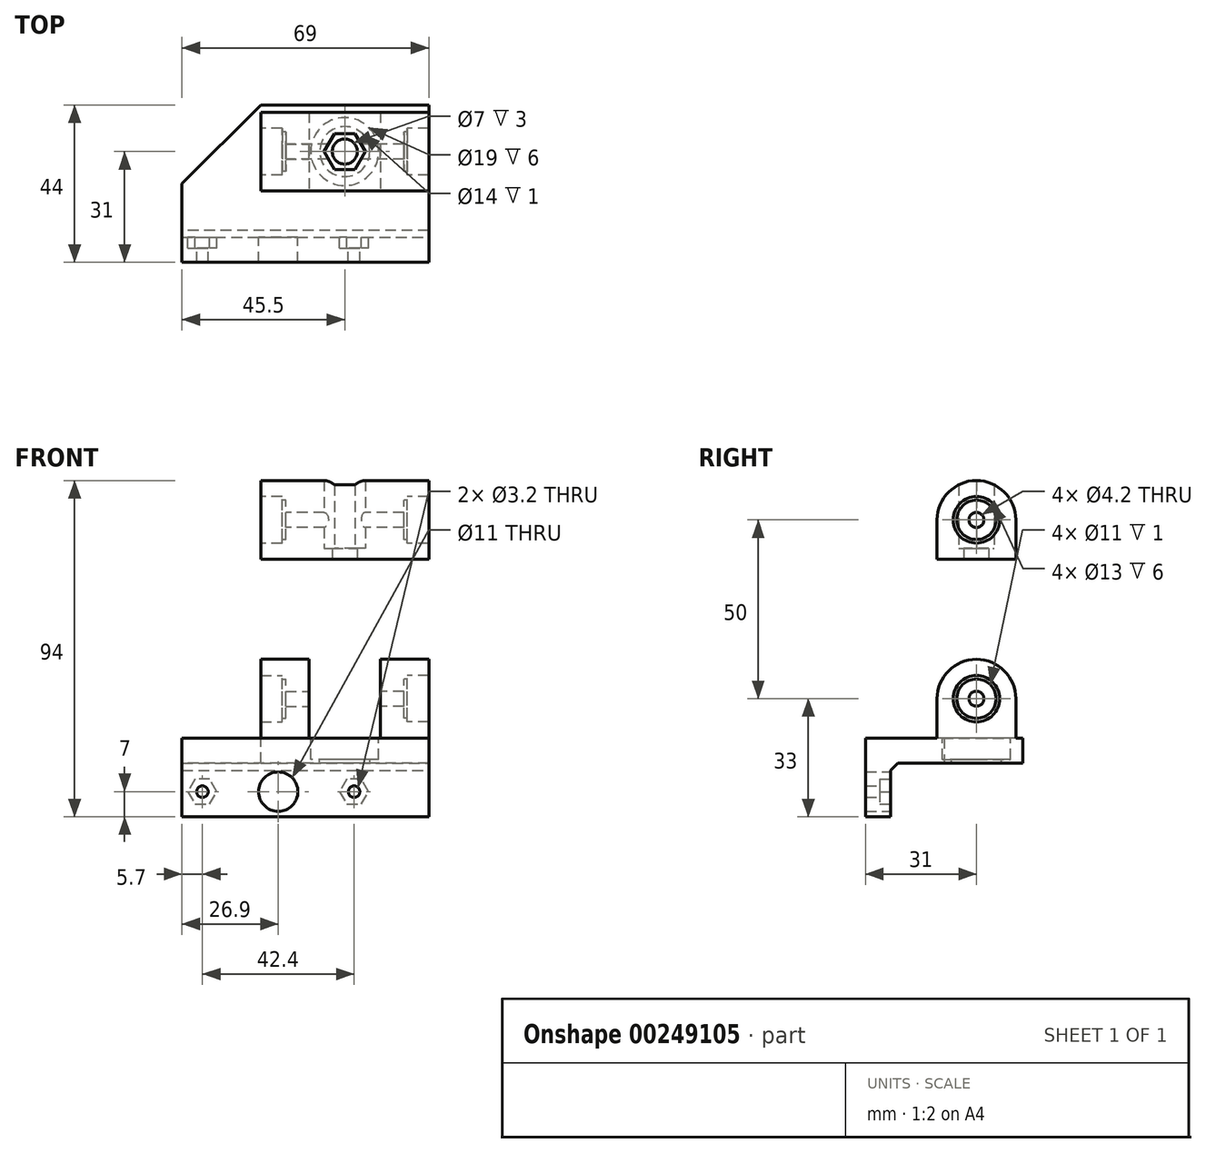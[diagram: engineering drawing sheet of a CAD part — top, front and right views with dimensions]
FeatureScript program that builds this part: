
annotation { "Feature Type Name" : "Feature", "Feature Type Description" : "" }
export const myFeature = defineFeature(function(context is Context, id is Id, definition is map)
    precondition{}
    {
        {
            var Q0;
            Q0=qCreatedBy(makeId("Top.planeOp"),FACE);
            var sketch = newSketch(context, id + "F0", { "sketchPlane" : qUnion([Q0])});
            skLineSegment(sketch, "E0", {"start": v(0, 0) * mm, "end": v(-23.5, 0) * mm, "construction": true});
            skLineSegment(sketch, "E1", {"start": v(0, 0) * mm, "end": v(23.5, 0) * mm, "construction": true});
            skLineSegment(sketch, "E2", {"start": v(-23.5, 0) * mm, "end": v(-23.5, -31) * mm});
            skLineSegment(sketch, "E3", {"start": v(-23.5, -31) * mm, "end": v(23.5, -31) * mm});
            skLineSegment(sketch, "E4", {"start": v(23.5, -31) * mm, "end": v(23.5, 0) * mm});
            skLineSegment(sketch, "E5", {"start": v(-23.5, 0) * mm, "end": v(-23.5, 13) * mm});
            skLineSegment(sketch, "E6", {"start": v(-23.5, 13) * mm, "end": v(23.5, 13) * mm});
            skLineSegment(sketch, "E7", {"start": v(23.5, 13) * mm, "end": v(23.5, 0) * mm});
            skCircle(sketch, "E8", {"center": v(0, 0) * mm, "radius": 9.5 * mm});
            skCircle(sketch, "E9", {"center": v(0, 0) * mm, "radius": 7 * mm});
            skLineSegment(sketch, "E10", {"start": v(0, 16.88) * mm, "end": v(-15, 16.88) * mm, "construction": true});
            skSolve(sketch);
        }
        {
            var Q0;
            Q0=makeQuery(id+"F0.imprint","IMPRINT",FACE,{"disambiguationData":[TD([[makeQuery(id+"F0.imprint","IMPRINT",EDGE,{"derivedFrom":sQuery(id+"F0.wireOp",EDGE,"E2")}),1.0]])]});
            extrude(context, id + "F1", {"entities" : qUnion([Q0]), "oppositeDirection" : true, "depth" : 7 * mm});
        }
        {
            var Q0;
            Q0=makeQuery(id+"F0.imprint","IMPRINT",FACE,{"disambiguationData":[TD([[makeQuery(id+"F0.imprint","IMPRINT",EDGE,{"derivedFrom":sQuery(id+"F0.wireOp",EDGE,"E8")}),1.0]])]});
            extrude(context, id + "F2", {"entities" : qUnion([Q0]), "operationType" : NewBodyOperationType.ADD, "oppositeDirection" : true, "depth" : 7 * mm, "hasSecondDirection" : true, "secondDirectionOppositeDirection" : true, "secondDirectionDepth" : 6 * mm});
        }
        {
            var Q0;
            {var subQ0=sQuery(id+"F0.wireOp",EDGE,"E8");Q0=makeQuery(id+"F2.boolean.opBoolean","MERGE",FACE,{"derivedFrom":[makeQuery(id+"F1.opExtrude","CAP_FACE",FACE,{"disambiguationData":[OSD([sQuery(id+"F0.wireOp",EDGE,"E2"),sQuery(id+"F0.wireOp",EDGE,"E3"),sQuery(id+"F0.wireOp",EDGE,"E4"),sQuery(id+"F0.wireOp",EDGE,"E5"),sQuery(id+"F0.wireOp",EDGE,"E6"),sQuery(id+"F0.wireOp",EDGE,"E7"),subQ0])],"isStart":false}),makeQuery(id+"F2.opExtrude","CAP_FACE",FACE,{"disambiguationData":[OSD([subQ0,sQuery(id+"F0.wireOp",EDGE,"E9")])],"isStart":false})]});}
            var sketch = newSketch(context, id + "F3", { "sketchPlane" : qUnion([Q0])});
            skLineSegment(sketch, "E11.bottom", {"start": v(-23.5, 31) * mm, "end": v(23.5, 31) * mm});
            skLineSegment(sketch, "E11.top", {"start": v(-23.5, 24) * mm, "end": v(23.5, 24) * mm});
            skLineSegment(sketch, "E11.left", {"start": v(-23.5, 31) * mm, "end": v(-23.5, 24) * mm});
            skLineSegment(sketch, "E11.right", {"start": v(23.5, 31) * mm, "end": v(23.5, 24) * mm});
            skSolve(sketch);
        }
        {
            var Q0;
            Q0 = qSketchRegion(id + "F3", true);
            extrude(context, id + "F4", {"entities" : qUnion([Q0]), "operationType" : NewBodyOperationType.ADD, "depth" : 14 * mm});
        }
        {
            var Q0;
            Q0=makeQuery(id+"F4.opExtrude","SWEPT_FACE",FACE,{"disambiguationData":[OSD([sQuery(id+"F3.wireOp",EDGE,"E11.top")])]});
            var sketch = newSketch(context, id + "F5", { "sketchPlane" : qUnion([Q0])});
            skCircle(sketch, "E12", {"center": v(18.6, -15) * mm, "radius": 4.85 * mm});
            skCircle(sketch, "E13", {"center": v(39.8, -15) * mm, "radius": 1.6 * mm});
            skCircle(sketch, "E14", {"center": v(-2.6, -15) * mm, "radius": 1.6 * mm});
            skCircle(sketch, "E15", {"center": v(18.6, -15) * mm, "radius": 5.5 * mm});
            skSolve(sketch);
        }
        {
            var Q0;
            Q0=makeQuery(id+"F4.boolean.opBoolean","MERGE",FACE,{"derivedFrom":[makeQuery(id+"F1.opExtrude","SWEPT_FACE",FACE,{"disambiguationData":[OSD([sQuery(id+"F0.wireOp",EDGE,"E2"),sQuery(id+"F0.wireOp",EDGE,"E5")])]}),makeQuery(id+"F4.opExtrude","SWEPT_FACE",FACE,{"disambiguationData":[OSD([sQuery(id+"F3.wireOp",EDGE,"E11.left")])]})]});
            var sketch = newSketch(context, id + "F6", { "sketchPlane" : qUnion([Q0])});
            skLineSegment(sketch, "E16", {"start": v(24, -7) * mm, "end": v(31, -7) * mm});
            skSolve(sketch);
        }
        {
            var Q0;
            Q0 = qSketchRegion(id + "F6", true);
            var Q1;
            {var subQ0=sQuery(id+"F6.wireOp",EDGE,"E16");Q1=makeQuery(id+"F6.imprint","IMPRINT",FACE,{"disambiguationData":[TD([[makeQuery(id+"F6.imprint","IMPRINT",EDGE,{"derivedFrom":subQ0}),-1.0]])]});}
            extrude(context, id + "F7", {"entities" : qUnion([Q0, Q1]), "operationType" : NewBodyOperationType.ADD, "depth" : 22 * mm});
        }
        {
            var Q0;
            Q0=qCreatedBy(makeId("Right.planeOp"),FACE);
            var sketch = newSketch(context, id + "F8", { "sketchPlane" : qUnion([Q0])});
            skCircle(sketch, "E17", {"center": v(0, 11) * mm, "radius": 6.5 * mm});
            skCircle(sketch, "E18", {"center": v(0, 11) * mm, "radius": 11 * mm});
            skCircle(sketch, "E19", {"center": v(0, 11) * mm, "radius": 5.5 * mm});
            skLineSegment(sketch, "E20", {"start": v(11, 11) * mm, "end": v(11, 0) * mm});
            skLineSegment(sketch, "E21", {"start": v(-11, 11) * mm, "end": v(-11, 0) * mm});
            skCircle(sketch, "E22", {"center": v(0, 11) * mm, "radius": 2.1 * mm});
            skLineSegment(sketch, "E23", {"start": v(11, 0) * mm, "end": v(0, 0) * mm});
            skLineSegment(sketch, "E24", {"start": v(0, 0) * mm, "end": v(-11, 0) * mm});
            skSolve(sketch);
        }
        {
            var Q0;
            {var subQ0=sQuery(id+"F8.wireOp",EDGE,"E20");Q0=makeQuery(id+"F8.imprint","IMPRINT",FACE,{"disambiguationData":[TD([[makeQuery(id+"F8.imprint","IMPRINT",EDGE,{"derivedFrom":subQ0}),-1.0]])]});}
            var Q1;
            {var subQ0=sQuery(id+"F8.wireOp",EDGE,"E21");Q1=makeQuery(id+"F8.imprint","IMPRINT",FACE,{"disambiguationData":[TD([[makeQuery(id+"F8.imprint","IMPRINT",EDGE,{"derivedFrom":subQ0}),1.0]])]});}
            var Q2;
            Q2=makeQuery(id+"F8.imprint","IMPRINT",FACE,{"disambiguationData":[TD([[makeQuery(id+"F8.imprint","IMPRINT",EDGE,{"derivedFrom":sQuery(id+"F8.wireOp",EDGE,"E17")}),-1.0]])]});
            extrude(context, id + "F9", {"entities" : qUnion([Q0, Q1, Q2]), "operationType" : NewBodyOperationType.ADD, "depth" : 23.5 * mm, "hasSecondDirection" : true, "secondDirectionOppositeDirection" : false, "secondDirectionDepth" : 10 * mm});
        }
        {
            var Q0;
            {var subQ0=sQuery(id+"F8.wireOp",EDGE,"E21");Q0=makeQuery(id+"F8.imprint","IMPRINT",FACE,{"disambiguationData":[TD([[makeQuery(id+"F8.imprint","IMPRINT",EDGE,{"derivedFrom":subQ0}),1.0]])]});}
            var Q1;
            {var subQ0=sQuery(id+"F8.wireOp",EDGE,"E20");Q1=makeQuery(id+"F8.imprint","IMPRINT",FACE,{"disambiguationData":[TD([[makeQuery(id+"F8.imprint","IMPRINT",EDGE,{"derivedFrom":subQ0}),-1.0]])]});}
            var Q2;
            Q2=makeQuery(id+"F8.imprint","IMPRINT",FACE,{"disambiguationData":[TD([[makeQuery(id+"F8.imprint","IMPRINT",EDGE,{"derivedFrom":sQuery(id+"F8.wireOp",EDGE,"E17")}),-1.0]])]});
            extrude(context, id + "F10", {"entities" : qUnion([Q0, Q1, Q2]), "operationType" : NewBodyOperationType.ADD, "oppositeDirection" : true, "depth" : 23.5 * mm, "hasSecondDirection" : true, "secondDirectionOppositeDirection" : true, "secondDirectionDepth" : 10 * mm});
        }
        {
            var Q0;
            Q0=makeQuery(id+"F8.imprint","IMPRINT",FACE,{"disambiguationData":[TD([[makeQuery(id+"F8.imprint","IMPRINT",EDGE,{"derivedFrom":sQuery(id+"F8.wireOp",EDGE,"E17")}),1.0]])]});
            extrude(context, id + "F11", {"entities" : qUnion([Q0]), "operationType" : NewBodyOperationType.ADD, "depth" : (23.5 - 6) * mm, "hasSecondDirection" : true, "secondDirectionOppositeDirection" : false, "secondDirectionDepth" : 10 * mm});
        }
        {
            var Q0;
            Q0=makeQuery(id+"F8.imprint","IMPRINT",FACE,{"disambiguationData":[TD([[makeQuery(id+"F8.imprint","IMPRINT",EDGE,{"derivedFrom":sQuery(id+"F8.wireOp",EDGE,"E17")}),1.0]])]});
            extrude(context, id + "F12", {"entities" : qUnion([Q0]), "operationType" : NewBodyOperationType.ADD, "oppositeDirection" : true, "depth" : 17.5 * mm, "hasSecondDirection" : true, "secondDirectionOppositeDirection" : true, "secondDirectionDepth" : 10 * mm});
        }
        {
            var Q0;
            Q0=makeQuery(id+"F8.imprint","IMPRINT",FACE,{"disambiguationData":[TD([[makeQuery(id+"F8.imprint","IMPRINT",EDGE,{"derivedFrom":sQuery(id+"F8.wireOp",EDGE,"E19")}),1.0]])]});
            extrude(context, id + "F13", {"entities" : qUnion([Q0]), "operationType" : NewBodyOperationType.ADD, "oppositeDirection" : true, "depth" : 16.5 * mm, "hasSecondDirection" : true, "secondDirectionOppositeDirection" : true, "secondDirectionDepth" : 10 * mm});
        }
        {
            var Q0;
            Q0=makeQuery(id+"F10.boolean.opBoolean","MERGE",FACE,{"derivedFrom":[makeQuery(id+"F4.boolean.opBoolean","MERGE",FACE,{"derivedFrom":[makeQuery(id+"F1.opExtrude","SWEPT_FACE",FACE,{"disambiguationData":[OSD([sQuery(id+"F0.wireOp",EDGE,"E2"),sQuery(id+"F0.wireOp",EDGE,"E5")])]}),makeQuery(id+"F4.opExtrude","SWEPT_FACE",FACE,{"disambiguationData":[OSD([sQuery(id+"F3.wireOp",EDGE,"E11.left")])]})]}),makeQuery(id+"F10.opExtrude","CAP_FACE",FACE,{"disambiguationData":[OSD([sQuery(id+"F8.wireOp",EDGE,"E17"),sQuery(id+"F8.wireOp",EDGE,"E18"),sQuery(id+"F8.wireOp",EDGE,"E20"),sQuery(id+"F8.wireOp",EDGE,"E21"),sQuery(id+"F8.wireOp",EDGE,"E23"),sQuery(id+"F8.wireOp",EDGE,"E24")])],"isStart":false})]});
            var sketch = newSketch(context, id + "F14", { "sketchPlane" : qUnion([Q0])});
            skLineSegment(sketch, "E25.bottom", {"start": v(-13, 0) * mm, "end": v(31, 0) * mm});
            skLineSegment(sketch, "E25.top", {"start": v(-13, -7) * mm, "end": v(31, -7) * mm});
            skLineSegment(sketch, "E25.left", {"start": v(-13, 0) * mm, "end": v(-13, -7) * mm});
            skLineSegment(sketch, "E25.right", {"start": v(31, 0) * mm, "end": v(31, -7) * mm});
            skSolve(sketch);
        }
        {
            var Q0;
            {var subQ0=sQuery(id+"F14.wireOp",EDGE,"E25.left");Q0=makeQuery(id+"F14.imprint","IMPRINT",FACE,{"disambiguationData":[TD([[makeQuery(id+"F14.imprint","IMPRINT",EDGE,{"derivedFrom":subQ0}),-1.0]])]});}
            extrude(context, id + "F15", {"entities" : qUnion([Q0]), "operationType" : NewBodyOperationType.ADD, "depth" : 22 * mm});
        }
        {
            var Q0;
            Q0=makeQuery(id+"F5.imprint","IMPRINT",FACE,{"disambiguationData":[TD([[makeQuery(id+"F5.imprint","IMPRINT",EDGE,{"derivedFrom":sQuery(id+"F5.wireOp",EDGE,"E14")}),1.0]])]});
            var Q1;
            Q1=makeQuery(id+"F5.imprint","IMPRINT",FACE,{"disambiguationData":[TD([[makeQuery(id+"F5.imprint","IMPRINT",EDGE,{"derivedFrom":sQuery(id+"F5.wireOp",EDGE,"E13")}),1.0]])]});
            var Q2;
            Q2=makeQuery(id+"F5.imprint","IMPRINT",FACE,{"disambiguationData":[TD([[makeQuery(id+"F5.imprint","IMPRINT",EDGE,{"derivedFrom":sQuery(id+"F5.wireOp",EDGE,"E12")}),-1.0]])]});
            var Q3;
            Q3=makeQuery(id+"F5.imprint","IMPRINT",FACE,{"disambiguationData":[TD([[makeQuery(id+"F5.imprint","IMPRINT",EDGE,{"derivedFrom":sQuery(id+"F5.wireOp",EDGE,"E12")}),1.0]])]});
            var Q4;
            {var subQ0=sQuery(id+"F5.wireOp",EDGE,"E15");var subQ1=makeQuery(id+"F4.opExtrude","SWEPT_EDGE",EDGE,{"disambiguationData":[OSD([sQuery(id+"F0.wireOp",EDGE,"E2"),sQuery(id+"F0.wireOp",EDGE,"E5"),sQuery(id+"F3.wireOp",EDGE,"E11.top"),sQuery(id+"F3.wireOp",EDGE,"E11.left")])]});var subQ2=makeQuery(id+"F5.imprint","INTERSECT",VERTEX,{"disambiguationData":[OD(0.0)],"derivedFrom":[subQ1,subQ0]});Q4=makeQuery(id+"F5.imprint","IMPRINT",FACE,{"disambiguationData":[TD([[makeQuery(id+"F5.imprint","IMPRINT",EDGE,{"disambiguationData":[TD([[subQ2,-1.0]])],"derivedFrom":subQ0}),1.0]])]});}
            extrude(context, id + "F16", {"entities" : qUnion([Q0, Q1, Q2, Q3, Q4]), "operationType" : NewBodyOperationType.REMOVE, "oppositeDirection" : true, "depth" : 25 * mm});
        }
        {
            var Q0;
            {var subQ0=sQuery(id+"F3.wireOp",EDGE,"E11.top");Q0=makeQuery(id+"F7.boolean.opBoolean","MERGE",FACE,{"derivedFrom":[makeQuery(id+"F4.opExtrude","SWEPT_FACE",FACE,{"disambiguationData":[OSD([subQ0])]}),makeQuery(id+"F7.opExtrude","SWEPT_FACE",FACE,{"disambiguationData":[OSD([sQuery(id+"F0.wireOp",EDGE,"E2"),sQuery(id+"F0.wireOp",EDGE,"E5"),subQ0,sQuery(id+"F3.wireOp",EDGE,"E11.left")])]})]});}
            var sketch = newSketch(context, id + "F17", { "sketchPlane" : qUnion([Q0])});
            skCircle(sketch, "E26.cCircle", {"center": v(-2.6, -15) * mm, "radius": 3.5 * mm, "construction": true});
            skLineSegment(sketch, "E26.0", {"start": v(-0.58, -18.5) * mm, "end": v(-4.62, -18.5) * mm});
            skLineSegment(sketch, "E26.1", {"start": v(-4.62, -18.5) * mm, "end": v(-6.64, -15) * mm});
            skLineSegment(sketch, "E26.2", {"start": v(-6.64, -15) * mm, "end": v(-4.62, -11.5) * mm});
            skLineSegment(sketch, "E26.3", {"start": v(-4.62, -11.5) * mm, "end": v(-0.58, -11.5) * mm});
            skLineSegment(sketch, "E26.4", {"start": v(-0.58, -11.5) * mm, "end": v(1.44, -15) * mm});
            skLineSegment(sketch, "E26.5", {"start": v(1.44, -15) * mm, "end": v(-0.58, -18.5) * mm});
            skPoint(sketch, "E26.0.midPoint", {"position": v(-2.6, -18.5) * mm});
            skCircle(sketch, "E27.cCircle", {"center": v(39.8, -15) * mm, "radius": 3.5 * mm, "construction": true});
            skLineSegment(sketch, "E27.0", {"start": v(41.82, -18.5) * mm, "end": v(37.78, -18.5) * mm});
            skLineSegment(sketch, "E27.1", {"start": v(37.78, -18.5) * mm, "end": v(35.76, -15) * mm});
            skLineSegment(sketch, "E27.2", {"start": v(35.76, -15) * mm, "end": v(37.78, -11.5) * mm});
            skLineSegment(sketch, "E27.3", {"start": v(37.78, -11.5) * mm, "end": v(41.82, -11.5) * mm});
            skLineSegment(sketch, "E27.4", {"start": v(41.82, -11.5) * mm, "end": v(43.84, -15) * mm});
            skLineSegment(sketch, "E27.5", {"start": v(43.84, -15) * mm, "end": v(41.82, -18.5) * mm});
            skPoint(sketch, "E27.0.midPoint", {"position": v(39.8, -18.5) * mm});
            skSolve(sketch);
        }
        {
            var Q0;
            Q0=makeQuery(id+"F17.imprint","IMPRINT",FACE,{"disambiguationData":[TD([[makeQuery(id+"F17.imprint","IMPRINT",EDGE,{"derivedFrom":sQuery(id+"F17.wireOp",EDGE,"E26.0")}),-1.0]])]});
            var Q1;
            Q1=makeQuery(id+"F17.imprint","IMPRINT",FACE,{"disambiguationData":[TD([[makeQuery(id+"F17.imprint","IMPRINT",EDGE,{"derivedFrom":sQuery(id+"F17.wireOp",EDGE,"E27.0")}),-1.0]])]});
            extrude(context, id + "F18", {"entities" : qUnion([Q0, Q1]), "operationType" : NewBodyOperationType.REMOVE, "oppositeDirection" : true, "depth" : 3 * mm});
        }
        {
            var Q0;
            {var subQ0=sQuery(id+"F3.wireOp",EDGE,"E11.left");Q0=makeQuery(id+"F7.boolean.opBoolean","MERGE",FACE,{"derivedFrom":[makeQuery(id+"F4.opExtrude","CAP_FACE",FACE,{"disambiguationData":[OSD([sQuery(id+"F3.wireOp",EDGE,"E11.bottom"),sQuery(id+"F3.wireOp",EDGE,"E11.top"),subQ0,sQuery(id+"F3.wireOp",EDGE,"E11.right")])],"isStart":false}),makeQuery(id+"F7.opExtrude","SWEPT_FACE",FACE,{"disambiguationData":[OSD([subQ0])]})]});}
            extrude(context, id + "F19", {"entities" : qUnion([Q0]), "operationType" : NewBodyOperationType.ADD, "depth" : 1 * mm});
        }
        {
            var Q0;
            {var subQ0=sQuery(id+"F3.wireOp",EDGE,"E11.top");Q0=makeQuery(id+"F15.boolean.opBoolean","MERGE",EDGE,{"derivedFrom":[makeQuery(id+"F4.opExtrude","CAP_EDGE",EDGE,{"disambiguationData":[OSD([subQ0])],"isStart":true}),makeQuery(id+"F7.opExtrude","SWEPT_EDGE",EDGE,{"disambiguationData":[OSD([sQuery(id+"F0.wireOp",EDGE,"E2"),sQuery(id+"F0.wireOp",EDGE,"E5"),subQ0,sQuery(id+"F3.wireOp",EDGE,"E11.left"),sQuery(id+"F6.wireOp",EDGE,"E16")])]})]});}
            var Q1;
            Q1=makeQuery(id+"F10.opExtrude","SWEPT_EDGE",EDGE,{"disambiguationData":[OSD([sQuery(id+"F8.wireOp",EDGE,"E20"),sQuery(id+"F8.wireOp",EDGE,"E23")])]});
            var Q2;
            Q2=makeQuery(id+"F9.opExtrude","SWEPT_EDGE",EDGE,{"disambiguationData":[OSD([sQuery(id+"F8.wireOp",EDGE,"E20"),sQuery(id+"F8.wireOp",EDGE,"E23")])]});
            var Q3;
            Q3=makeQuery(id+"F9.opExtrude","SWEPT_EDGE",EDGE,{"disambiguationData":[OSD([sQuery(id+"F8.wireOp",EDGE,"E21"),sQuery(id+"F8.wireOp",EDGE,"E24")])]});
            var Q4;
            Q4=makeQuery(id+"F10.opExtrude","SWEPT_EDGE",EDGE,{"disambiguationData":[OSD([sQuery(id+"F8.wireOp",EDGE,"E21"),sQuery(id+"F8.wireOp",EDGE,"E24")])]});
            chamfer(context, id + "F20", {"entities" : qUnion([Q0, Q1, Q2, Q3, Q4]), "width" : 2 * mm, "tangentPropagation" : true});
        }
        {
            var Q0;
            Q0=makeQuery(id+"F15.opExtrude","CAP_EDGE",EDGE,{"disambiguationData":[OSD([sQuery(id+"F14.wireOp",EDGE,"E25.left")])],"isStart":false});
            chamfer(context, id + "F21", {"entities" : qUnion([Q0]), "width" : 22 * mm, "tangentPropagation" : true});
        }
        {
            var Q0;
            Q0=qCreatedBy(makeId("Right.planeOp"),FACE);
            var sketch = newSketch(context, id + "F22", { "sketchPlane" : qUnion([Q0])});
            skCircle(sketch, "E28", {"center": v(0, 61) * mm, "radius": 6.5 * mm});
            skCircle(sketch, "E29", {"center": v(0, 61) * mm, "radius": 11 * mm});
            skCircle(sketch, "E30", {"center": v(0, 61) * mm, "radius": 5.5 * mm});
            skLineSegment(sketch, "E31", {"start": v(11, 61) * mm, "end": v(11, 50) * mm});
            skLineSegment(sketch, "E32", {"start": v(-11, 61) * mm, "end": v(-11, 50) * mm});
            skCircle(sketch, "E33", {"center": v(0, 61) * mm, "radius": 2.1 * mm});
            skLineSegment(sketch, "E34", {"start": v(11, 50) * mm, "end": v(0, 50) * mm});
            skLineSegment(sketch, "E35", {"start": v(0, 50) * mm, "end": v(-11, 50) * mm});
            skLineSegment(sketch, "E36", {"start": v(0, 61) * mm, "end": v(0, 50) * mm, "construction": true});
            skSolve(sketch);
        }
        {
            var Q0;
            Q0=makeQuery(id+"F22.imprint","IMPRINT",FACE,{"disambiguationData":[TD([[makeQuery(id+"F22.imprint","IMPRINT",EDGE,{"derivedFrom":sQuery(id+"F22.wireOp",EDGE,"E28")}),-1.0]])]});
            var Q1;
            {var subQ0=sQuery(id+"F22.wireOp",EDGE,"E32");Q1=makeQuery(id+"F22.imprint","IMPRINT",FACE,{"disambiguationData":[TD([[makeQuery(id+"F22.imprint","IMPRINT",EDGE,{"derivedFrom":subQ0}),1.0]])]});}
            var Q2;
            {var subQ0=sQuery(id+"F22.wireOp",EDGE,"E31");Q2=makeQuery(id+"F22.imprint","IMPRINT",FACE,{"disambiguationData":[TD([[makeQuery(id+"F22.imprint","IMPRINT",EDGE,{"derivedFrom":subQ0}),-1.0]])]});}
            extrude(context, id + "F23", {"entities" : qUnion([Q0, Q1, Q2]), "endBound" : BoundingType.SYMMETRIC, "depth" : (23.5 * 2) * mm});
        }
        {
            var Q0;
            Q0=makeQuery(id+"F22.imprint","IMPRINT",FACE,{"disambiguationData":[TD([[makeQuery(id+"F22.imprint","IMPRINT",EDGE,{"derivedFrom":sQuery(id+"F22.wireOp",EDGE,"E28")}),1.0]])]});
            extrude(context, id + "F24", {"entities" : qUnion([Q0]), "operationType" : NewBodyOperationType.ADD, "endBound" : BoundingType.SYMMETRIC, "depth" : (17.5 * 2) * mm});
        }
        {
            var Q0;
            Q0=makeQuery(id+"F8.imprint","IMPRINT",FACE,{"disambiguationData":[TD([[makeQuery(id+"F8.imprint","IMPRINT",EDGE,{"derivedFrom":sQuery(id+"F8.wireOp",EDGE,"E19")}),1.0]])]});
            extrude(context, id + "F25", {"entities" : qUnion([Q0]), "operationType" : NewBodyOperationType.ADD, "depth" : 16.5 * mm, "hasSecondDirection" : true, "secondDirectionOppositeDirection" : false, "secondDirectionDepth" : 10 * mm});
        }
        {
            var Q0;
            Q0=makeQuery(id+"F22.imprint","IMPRINT",FACE,{"disambiguationData":[TD([[makeQuery(id+"F22.imprint","IMPRINT",EDGE,{"derivedFrom":sQuery(id+"F22.wireOp",EDGE,"E30")}),1.0]])]});
            extrude(context, id + "F26", {"entities" : qUnion([Q0]), "operationType" : NewBodyOperationType.ADD, "endBound" : BoundingType.SYMMETRIC, "depth" : (16.5 * 2) * mm});
        }
        {
            var Q0;
            Q0=makeQuery(id+"F23.opExtrude","SWEPT_FACE",FACE,{"disambiguationData":[OSD([sQuery(id+"F22.wireOp",EDGE,"E34"),sQuery(id+"F22.wireOp",EDGE,"E35")])]});
            var sketch = newSketch(context, id + "F27", { "sketchPlane" : qUnion([Q0])});
            skCircle(sketch, "E37", {"center": v(0, 0) * mm, "radius": 3.5 * mm});
            skCircle(sketch, "E38.cCircle", {"center": v(0, 0) * mm, "radius": 5 * mm, "construction": true});
            skLineSegment(sketch, "E38.0", {"start": v(2.89, -5) * mm, "end": v(-2.89, -5) * mm});
            skLineSegment(sketch, "E38.1", {"start": v(-2.89, -5) * mm, "end": v(-5.77, 0) * mm});
            skLineSegment(sketch, "E38.2", {"start": v(-5.77, 0) * mm, "end": v(-2.89, 5) * mm});
            skLineSegment(sketch, "E38.3", {"start": v(-2.89, 5) * mm, "end": v(2.89, 5) * mm});
            skLineSegment(sketch, "E38.4", {"start": v(2.89, 5) * mm, "end": v(5.77, 0) * mm});
            skLineSegment(sketch, "E38.5", {"start": v(5.77, 0) * mm, "end": v(2.89, -5) * mm});
            skPoint(sketch, "E38.0.midPoint", {"position": v(0, -5) * mm});
            skSolve(sketch);
        }
        {
            var Q0;
            Q0=makeQuery(id+"F27.imprint","IMPRINT",FACE,{"disambiguationData":[TD([[makeQuery(id+"F27.imprint","IMPRINT",EDGE,{"derivedFrom":sQuery(id+"F27.wireOp",EDGE,"E37")}),1.0]])]});
            var Q1;
            Q1=makeQuery(id+"F27.imprint","IMPRINT",FACE,{"disambiguationData":[TD([[makeQuery(id+"F27.imprint","IMPRINT",EDGE,{"derivedFrom":sQuery(id+"F27.wireOp",EDGE,"E37")}),-1.0]])]});
            extrude(context, id + "F28", {"entities" : qUnion([Q0, Q1]), "operationType" : NewBodyOperationType.REMOVE, "oppositeDirection" : true, "depth" : 25 * mm, "hasSecondDirection" : true, "secondDirectionOppositeDirection" : true, "secondDirectionDepth" : 3 * mm});
        }
        {
            var Q0;
            Q0=makeQuery(id+"F27.imprint","IMPRINT",FACE,{"disambiguationData":[TD([[makeQuery(id+"F27.imprint","IMPRINT",EDGE,{"derivedFrom":sQuery(id+"F27.wireOp",EDGE,"E37")}),1.0]])]});
            extrude(context, id + "F29", {"entities" : qUnion([Q0]), "operationType" : NewBodyOperationType.REMOVE, "oppositeDirection" : true, "depth" : 25 * mm});
        }
    });
